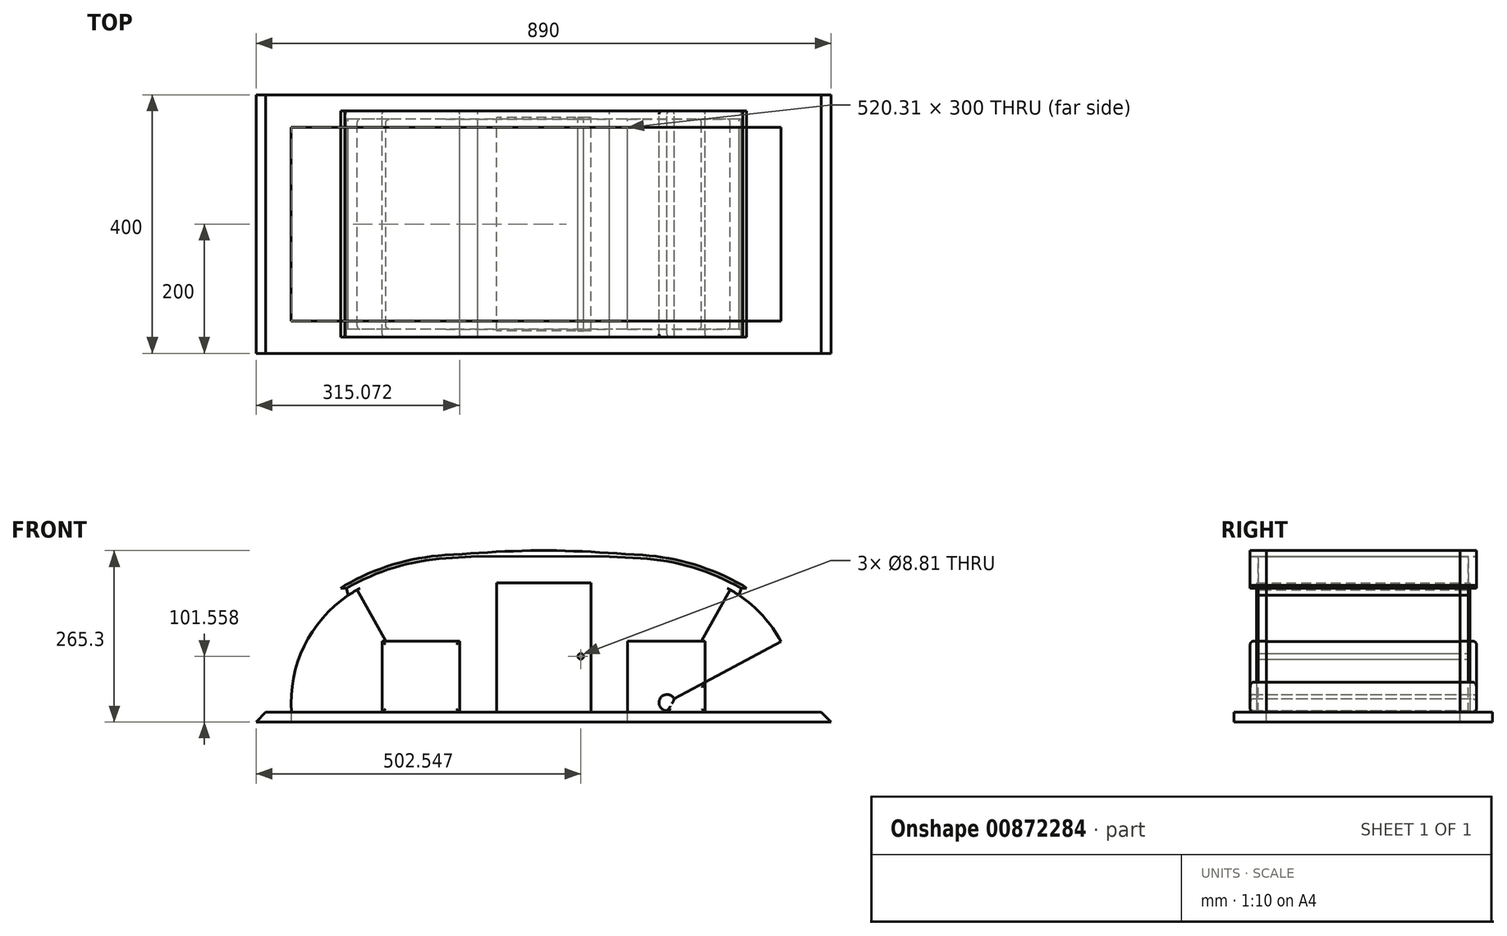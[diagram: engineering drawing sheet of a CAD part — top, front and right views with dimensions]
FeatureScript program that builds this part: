
annotation { "Feature Type Name" : "Feature", "Feature Type Description" : "" }
export const myFeature = defineFeature(function(context is Context, id is Id, definition is map)
    precondition{}
    {
        {
            var Q0;
            Q0=qCreatedBy(makeId("Front.planeOp"),FACE);
            var sketch = newSketch(context, id + "F0", { "sketchPlane" : qUnion([Q0])});
            skLineSegment(sketch, "E0.bottom", {"start": v(0.23, -0.16) * mm, "end": v(250.23, -0.16) * mm});
            skLineSegment(sketch, "E1", {"start": v(250.23, -0.16) * mm, "end": v(190.23, -0.16) * mm});
            skLineSegment(sketch, "E2", {"start": v(250.23, 257.8) * mm, "end": v(249.89, 257.87) * mm});
            skLineSegment(sketch, "E3.bottom", {"start": v(250.23, -0.16) * mm, "end": v(130.23, -0.16) * mm});
            skLineSegment(sketch, "E4", {"start": v(130.23, 109.84) * mm, "end": v(250.23, 109.84) * mm});
            skLineSegment(sketch, "E5", {"start": v(0.23, 199.84) * mm, "end": v(73.25, 199.84) * mm});
            skLineSegment(sketch, "E6", {"start": v(73.25, 199.84) * mm, "end": v(73.25, -0.16) * mm});
            skCircle(sketch, "E7", {"center": v(191.1, 14.84) * mm, "radius": 12.5 * mm});
            skCircle(sketch, "E8", {"center": v(57.55, 86.4) * mm, "radius": 4.4 * mm});
            skArc(sketch, "E9", {"start": v(390.54, -0.16) * mm, "mid": v(362.12, 118.54) * mm, "end": v(270.01, 198.62) * mm});
            skLineSegment(sketch, "E10", {"start": v(250.23, -0.16) * mm, "end": v(390.54, -0.16) * mm});
            skLineSegment(sketch, "E11", {"start": v(191.1, 14.84) * mm, "end": v(390.54, -0.16) * mm, "construction": true});
            skLineSegment(sketch, "E12", {"start": v(0.23, -0.16) * mm, "end": v(553.83, -0.16) * mm});
            skLineSegment(sketch, "E13", {"start": v(191.1, 14.84) * mm, "end": v(197.22, 25.74) * mm});
            skLineSegment(sketch, "E14", {"start": v(191.1, 14.84) * mm, "end": v(367.37, 109.35) * mm});
            skLineSegment(sketch, "E15", {"start": v(190.23, -0.16) * mm, "end": v(250.23, -0.16) * mm});
            skLineSegment(sketch, "E16", {"start": v(250.23, -0.16) * mm, "end": v(250.23, 109.84) * mm});
            skLineSegment(sketch, "E17", {"start": v(190.23, -0.16) * mm, "end": v(130.23, -0.16) * mm});
            skLineSegment(sketch, "E18", {"start": v(130.23, -0.16) * mm, "end": v(130.23, 109.84) * mm});
            skLineSegment(sketch, "E19", {"start": v(0.23, -0.16) * mm, "end": v(0.23, 199.84) * mm});
            skLineSegment(sketch, "E20", {"start": v(302.75, 180.78) * mm, "end": v(305.68, 191.63) * mm});
            skLineSegment(sketch, "E21", {"start": v(-4.12, 211.84) * mm, "end": v(-4.13, 211.84) * mm});
            skArc(sketch, "E22.trimOffspring", {"start": v(305.68, 191.63) * mm, "mid": v(230.69, 224.02) * mm, "end": v(150.23, 238.14) * mm});
            skLineSegment(sketch, "E23", {"start": v(191.1, 14.84) * mm, "end": v(191.1, -0.16) * mm});
            skLineSegment(sketch, "E24", {"start": v(298.85, 183.34) * mm, "end": v(250.23, 107.3) * mm, "construction": true});
            skLineSegment(sketch, "E25", {"start": v(191.1, 14.84) * mm, "end": v(184.4, 25.39) * mm, "construction": true});
            skLineSegment(sketch, "E26", {"start": v(83.85, 183.65) * mm, "end": v(84.52, 182.6) * mm});
            skLineSegment(sketch, "E27", {"start": v(0.23, 199.84) * mm, "end": v(0.23, 213.62) * mm});
            skLineSegment(sketch, "E28", {"start": v(270.01, 198.62) * mm, "end": v(298.76, 198.16) * mm, "construction": true});
            skLineSegment(sketch, "E29", {"start": v(305.68, 191.63) * mm, "end": v(314.05, 191.63) * mm});
            skArc(sketch, "E30.0", {"start": v(308.18, 195.95) * mm, "mid": v(233.4, 228.42) * mm, "end": v(153.2, 242.97) * mm});
            skLineSegment(sketch, "E31", {"start": v(308.18, 195.95) * mm, "end": v(314.05, 191.63) * mm});
            skLineSegment(sketch, "E32.MirrorCS", {"start": v(-72.8, 199.84) * mm, "end": v(-72.8, -0.16) * mm});
            skLineSegment(sketch, "E33.MirrorCS", {"start": v(0.23, 199.84) * mm, "end": v(-72.8, 199.84) * mm});
            skLineSegment(sketch, "E34.MirrorCS", {"start": v(0.23, -0.16) * mm, "end": v(-390.09, -0.16) * mm});
            skArc(sketch, "E35.MirrorCS", {"start": v(-390.09, -0.16) * mm, "mid": v(-366.89, 109.39) * mm, "end": v(-288.45, 189.3) * mm});
            skArc(sketch, "E36.MirrorCS", {"start": v(-307.73, 195.95) * mm, "mid": v(-232.95, 228.42) * mm, "end": v(-152.74, 242.97) * mm});
            skArc(sketch, "E37.MirrorCS", {"start": v(-305.22, 191.63) * mm, "mid": v(-231.06, 223.77) * mm, "end": v(-151.5, 238.04) * mm});
            skLineSegment(sketch, "E38.MirrorCS", {"start": v(-129.77, 109.84) * mm, "end": v(-249.77, 109.84) * mm});
            skLineSegment(sketch, "E39.MirrorCS", {"start": v(-129.77, -0.16) * mm, "end": v(-129.77, 109.84) * mm});
            skLineSegment(sketch, "E40.MirrorCS", {"start": v(-249.77, -0.16) * mm, "end": v(-249.77, 109.84) * mm});
            skLineSegment(sketch, "E41.MirrorCS", {"start": v(-249.77, 46.54) * mm, "end": v(-366.91, 109.35) * mm});
            skLineSegment(sketch, "E42.MirrorCS", {"start": v(-243.9, 109.84) * mm, "end": v(-288.45, 189.3) * mm});
            skFitSpline(sketch, "E43", {"points": [v(-152.74, 242.97) * mm, v(0, 250.14) * mm, v(153.2, 242.97) * mm], "startDerivative": vector(305.6, 21.52) * mm, "endDerivative": vector(306.28, -21.51) * mm});
            skLineSegment(sketch, "E44", {"start": v(150.23, 238.14) * mm, "end": v(102.11, 240.88) * mm});
            skLineSegment(sketch, "E45", {"start": v(-151.5, 238.04) * mm, "end": v(-101.85, 241.43) * mm});
            skLineSegment(sketch, "E46.MirrorCS", {"start": v(-302.3, 180.78) * mm, "end": v(-305.22, 191.63) * mm});
            skLineSegment(sketch, "E47.MirrorCS", {"start": v(-305.22, 191.63) * mm, "end": v(-313.6, 191.63) * mm});
            skLineSegment(sketch, "E48.MirrorCS", {"start": v(-307.73, 195.95) * mm, "end": v(-313.6, 191.63) * mm});
            skLineSegment(sketch, "E49", {"start": v(-101.85, 241.43) * mm, "end": v(102.11, 240.88) * mm});
            skPoint(sketch, "E50.MirrorCS.start.orphan", {"position": v(-298.39, 183.34) * mm});
            skLineSegment(sketch, "E51.trimOffspring", {"start": v(84.52, 182.6) * mm, "end": v(83.85, 183.65) * mm, "construction": true});
            skLineSegment(sketch, "E52.trimOffspring", {"start": v(197.84, 25.37) * mm, "end": v(191.1, 14.84) * mm, "construction": true});
            skLineSegment(sketch, "E53.trimOffspring", {"start": v(244.36, 109.84) * mm, "end": v(288.9, 189.3) * mm});
            skPoint(sketch, "E54.end.orphan", {"position": v(293.87, 198.16) * mm});
            skPoint(sketch, "E55.orphan", {"position": v(-553.37, -0.16) * mm});
            skSolve(sketch);
        }
        {
            var Q0;
            Q0=makeQuery(id+"F0.imprint","IMPRINT",FACE,{"disambiguationData":[TD([[makeQuery(id+"F0.imprint","IMPRINT",EDGE,{"derivedFrom":sQuery(id+"F0.wireOp",EDGE,"E5")}),1.0]])]});
            var Q1;
            {var subQ0=sQuery(id+"F0.wireOp",EDGE,"E39.MirrorCS");Q1=makeQuery(id+"F0.imprint","IMPRINT",FACE,{"disambiguationData":[TD([[makeQuery(id+"F0.imprint","IMPRINT",EDGE,{"derivedFrom":subQ0}),1.0]])]});}
            var Q2;
            {var subQ3=sQuery(id+"F0.wireOp",EDGE,"E41.MirrorCS");Q2=makeQuery(id+"F0.imprint","IMPRINT",FACE,{"disambiguationData":[TD([[makeQuery(id+"F0.imprint","IMPRINT",EDGE,{"derivedFrom":subQ3}),-1.0]])]});}
            var Q3;
            {var subQ5=sQuery(id+"F0.wireOp",EDGE,"E41.MirrorCS");Q3=makeQuery(id+"F0.imprint","IMPRINT",FACE,{"disambiguationData":[TD([[makeQuery(id+"F0.imprint","IMPRINT",EDGE,{"derivedFrom":subQ5}),1.0]])]});}
            var Q4;
            Q4=makeQuery(id+"F0.imprint","IMPRINT",FACE,{"disambiguationData":[TD([[makeQuery(id+"F0.imprint","IMPRINT",EDGE,{"derivedFrom":sQuery(id+"F0.wireOp",EDGE,"E5")}),-1.0]])]});
            var Q5;
            {var subQ0=sQuery(id+"F0.wireOp",EDGE,"E19");Q5=makeQuery(id+"F0.imprint","IMPRINT",FACE,{"disambiguationData":[TD([[makeQuery(id+"F0.imprint","IMPRINT",EDGE,{"derivedFrom":subQ0}),1.0]])]});}
            var Q6;
            {var subQ3=sQuery(id+"F0.wireOp",EDGE,"E53.trimOffspring");Q6=makeQuery(id+"F0.imprint","IMPRINT",FACE,{"disambiguationData":[TD([[makeQuery(id+"F0.imprint","IMPRINT",EDGE,{"derivedFrom":subQ3}),1.0]])]});}
            var Q7;
            {var subQ6=sQuery(id+"F0.wireOp",EDGE,"E53.trimOffspring");Q7=makeQuery(id+"F0.imprint","IMPRINT",FACE,{"disambiguationData":[TD([[makeQuery(id+"F0.imprint","IMPRINT",EDGE,{"derivedFrom":subQ6}),-1.0]])]});}
            var Q8;
            {var subQ0=sQuery(id+"F0.wireOp",EDGE,"E12");var subQ1=sQuery(id+"F0.wireOp",EDGE,"E9");var subQ2=makeQuery(id+"F0.imprint","INTERSECT",VERTEX,{"derivedFrom":[subQ1,subQ0]});Q8=makeQuery(id+"F0.imprint","IMPRINT",FACE,{"disambiguationData":[TD([[makeQuery(id+"F0.imprint","IMPRINT",EDGE,{"disambiguationData":[TD([[subQ2,-1.0]])],"derivedFrom":subQ1}),1.0]])]});}
            var Q9;
            {var subQ5=sQuery(id+"F0.wireOp",EDGE,"E17");Q9=makeQuery(id+"F0.imprint","IMPRINT",FACE,{"disambiguationData":[TD([[makeQuery(id+"F0.imprint","IMPRINT",EDGE,{"derivedFrom":subQ5}),-1.0]])]});}
            var Q10;
            {var subQ0=sQuery(id+"F0.wireOp",EDGE,"E13");Q10=makeQuery(id+"F0.imprint","IMPRINT",FACE,{"disambiguationData":[TD([[makeQuery(id+"F0.imprint","IMPRINT",EDGE,{"derivedFrom":subQ0}),1.0]])]});}
            var Q11;
            {var subQ0=sQuery(id+"F0.wireOp",EDGE,"E13");Q11=makeQuery(id+"F0.imprint","IMPRINT",FACE,{"disambiguationData":[TD([[makeQuery(id+"F0.imprint","IMPRINT",EDGE,{"derivedFrom":subQ0}),-1.0]])]});}
            var Q12;
            {var subQ0=sQuery(id+"F0.wireOp",EDGE,"E14");var subQ1=sQuery(id+"F0.wireOp",EDGE,"E7");var subQ2=makeQuery(id+"F0.imprint","INTERSECT",VERTEX,{"derivedFrom":[subQ1,subQ0]});Q12=makeQuery(id+"F0.imprint","IMPRINT",FACE,{"disambiguationData":[TD([[makeQuery(id+"F0.imprint","IMPRINT",EDGE,{"disambiguationData":[TD([[subQ2,1.0]])],"derivedFrom":subQ1}),1.0]])]});}
            var Q13;
            {var subQ5=sQuery(id+"F0.wireOp",EDGE,"E14");var subQ6=sQuery(id+"F0.wireOp",EDGE,"E7");var subQ7=makeQuery(id+"F0.imprint","INTERSECT",VERTEX,{"derivedFrom":[subQ6,subQ5]});Q13=makeQuery(id+"F0.imprint","IMPRINT",FACE,{"disambiguationData":[TD([[makeQuery(id+"F0.imprint","IMPRINT",EDGE,{"disambiguationData":[TD([[subQ7,1.0]])],"derivedFrom":subQ6}),-1.0]])]});}
            var Q14;
            {var subQ1=sQuery(id+"F0.wireOp",EDGE,"E20");Q14=makeQuery(id+"F0.imprint","IMPRINT",FACE,{"disambiguationData":[TD([[makeQuery(id+"F0.imprint","IMPRINT",EDGE,{"derivedFrom":subQ1}),1.0]])]});}
            var Q15;
            Q15=makeQuery(id+"F0.imprint","IMPRINT",FACE,{"disambiguationData":[TD([[makeQuery(id+"F0.imprint","IMPRINT",EDGE,{"derivedFrom":sQuery(id+"F0.wireOp",EDGE,"E22.trimOffspring")}),-1.0]])]});
            extrude(context, id + "F1", {"entities" : qUnion([Q0, Q1, Q2, Q3, Q4, Q5, Q6, Q7, Q8, Q9, Q10, Q11, Q12, Q13, Q14, Q15]), "endBound" : BoundingType.SYMMETRIC, "depth" : 300 * mm, "offsetDistance" : 25 * mm});
        }
        {
            var Q0;
            Q0=makeQuery(id+"F0.imprint","IMPRINT",FACE,{"disambiguationData":[TD([[makeQuery(id+"F0.imprint","IMPRINT",EDGE,{"derivedFrom":sQuery(id+"F0.wireOp",EDGE,"E22.trimOffspring")}),-1.0]])]});
            extrude(context, id + "F2", {"entities" : qUnion([Q0]), "endBound" : BoundingType.SYMMETRIC, "depth" : 350 * mm, "offsetDistance" : 25 * mm});
        }
        {
            var Q0;
            {var subQ0=sQuery(id+"F0.wireOp",EDGE,"E39.MirrorCS");Q0=makeQuery(id+"F0.imprint","IMPRINT",FACE,{"disambiguationData":[TD([[makeQuery(id+"F0.imprint","IMPRINT",EDGE,{"derivedFrom":subQ0}),1.0]])]});}
            var Q1;
            {var subQ5=sQuery(id+"F0.wireOp",EDGE,"E17");Q1=makeQuery(id+"F0.imprint","IMPRINT",FACE,{"disambiguationData":[TD([[makeQuery(id+"F0.imprint","IMPRINT",EDGE,{"derivedFrom":subQ5}),-1.0]])]});}
            var Q2;
            {var subQ5=sQuery(id+"F0.wireOp",EDGE,"E14");var subQ6=sQuery(id+"F0.wireOp",EDGE,"E7");var subQ7=makeQuery(id+"F0.imprint","INTERSECT",VERTEX,{"derivedFrom":[subQ6,subQ5]});Q2=makeQuery(id+"F0.imprint","IMPRINT",FACE,{"disambiguationData":[TD([[makeQuery(id+"F0.imprint","IMPRINT",EDGE,{"disambiguationData":[TD([[subQ7,1.0]])],"derivedFrom":subQ6}),-1.0]])]});}
            var Q3;
            {var subQ0=sQuery(id+"F0.wireOp",EDGE,"E13");Q3=makeQuery(id+"F0.imprint","IMPRINT",FACE,{"disambiguationData":[TD([[makeQuery(id+"F0.imprint","IMPRINT",EDGE,{"derivedFrom":subQ0}),1.0]])]});}
            var Q4;
            {var subQ0=sQuery(id+"F0.wireOp",EDGE,"E14");var subQ1=sQuery(id+"F0.wireOp",EDGE,"E7");var subQ2=makeQuery(id+"F0.imprint","INTERSECT",VERTEX,{"derivedFrom":[subQ1,subQ0]});Q4=makeQuery(id+"F0.imprint","IMPRINT",FACE,{"disambiguationData":[TD([[makeQuery(id+"F0.imprint","IMPRINT",EDGE,{"disambiguationData":[TD([[subQ2,1.0]])],"derivedFrom":subQ1}),1.0]])]});}
            var Q5;
            {var subQ0=sQuery(id+"F0.wireOp",EDGE,"E13");Q5=makeQuery(id+"F0.imprint","IMPRINT",FACE,{"disambiguationData":[TD([[makeQuery(id+"F0.imprint","IMPRINT",EDGE,{"derivedFrom":subQ0}),-1.0]])]});}
            extrude(context, id + "F3", {"entities" : qUnion([Q0, Q1, Q2, Q3, Q4, Q5]), "endBound" : BoundingType.SYMMETRIC, "depth" : 350 * mm, "offsetDistance" : 25 * mm});
        }
        {
            var Q0;
            {var subQ0=sQuery(id+"F0.wireOp",EDGE,"E19");Q0=makeQuery(id+"F0.imprint","IMPRINT",FACE,{"disambiguationData":[TD([[makeQuery(id+"F0.imprint","IMPRINT",EDGE,{"derivedFrom":subQ0}),1.0]])]});}
            var Q1;
            Q1=makeQuery(id+"F0.imprint","IMPRINT",FACE,{"disambiguationData":[TD([[makeQuery(id+"F0.imprint","IMPRINT",EDGE,{"derivedFrom":sQuery(id+"F0.wireOp",EDGE,"E5")}),-1.0]])]});
            var Q2;
            Q2=makeQuery(id+"F0.imprint","IMPRINT",FACE,{"disambiguationData":[TD([[makeQuery(id+"F0.imprint","IMPRINT",EDGE,{"derivedFrom":sQuery(id+"F0.wireOp",EDGE,"E5")}),1.0]])]});
            var Q3;
            {var subQ1=sQuery(id+"F0.wireOp",EDGE,"E20");Q3=makeQuery(id+"F0.imprint","IMPRINT",FACE,{"disambiguationData":[TD([[makeQuery(id+"F0.imprint","IMPRINT",EDGE,{"derivedFrom":subQ1}),1.0]])]});}
            var Q4;
            {var subQ3=sQuery(id+"F0.wireOp",EDGE,"E53.trimOffspring");Q4=makeQuery(id+"F0.imprint","IMPRINT",FACE,{"disambiguationData":[TD([[makeQuery(id+"F0.imprint","IMPRINT",EDGE,{"derivedFrom":subQ3}),1.0]])]});}
            extrude(context, id + "F4", {"entities" : qUnion([Q0, Q1, Q2, Q3, Q4]), "endBound" : BoundingType.SYMMETRIC, "depth" : 325 * mm, "offsetDistance" : 25 * mm});
        }
        {
            var Q0;
            {var subQ0=sQuery(id+"F0.wireOp",EDGE,"E19");Q0=makeQuery(id+"F0.imprint","IMPRINT",FACE,{"disambiguationData":[TD([[makeQuery(id+"F0.imprint","IMPRINT",EDGE,{"derivedFrom":subQ0}),1.0]])]});}
            var Q1;
            Q1=makeQuery(id+"F0.imprint","IMPRINT",FACE,{"disambiguationData":[TD([[makeQuery(id+"F0.imprint","IMPRINT",EDGE,{"derivedFrom":sQuery(id+"F0.wireOp",EDGE,"E5")}),-1.0]])]});
            extrude(context, id + "F5", {"entities" : qUnion([Q0, Q1]), "endBound" : BoundingType.SYMMETRIC, "depth" : 330 * mm, "offsetDistance" : 25 * mm});
        }
        {
            var Q0;
            Q0=makeQuery(id+"F3.opExtrude","CAP_FACE",FACE,{"disambiguationData":[OSD([sQuery(id+"F0.wireOp",EDGE,"E4"),sQuery(id+"F0.wireOp",EDGE,"E15"),sQuery(id+"F0.wireOp",EDGE,"E16"),sQuery(id+"F0.wireOp",EDGE,"E17"),sQuery(id+"F0.wireOp",EDGE,"E18")])],"isStart":true});
            var Q1;
            Q1=makeQuery(id+"F3.opExtrude","CAP_FACE",FACE,{"disambiguationData":[OSD([sQuery(id+"F0.wireOp",EDGE,"E34.MirrorCS"),sQuery(id+"F0.wireOp",EDGE,"E38.MirrorCS"),sQuery(id+"F0.wireOp",EDGE,"E39.MirrorCS"),sQuery(id+"F0.wireOp",EDGE,"E40.MirrorCS")])],"isStart":true});
            var Q2;
            Q2=makeQuery(id+"F3.opExtrude","CAP_FACE",FACE,{"disambiguationData":[OSD([sQuery(id+"F0.wireOp",EDGE,"E34.MirrorCS"),sQuery(id+"F0.wireOp",EDGE,"E38.MirrorCS"),sQuery(id+"F0.wireOp",EDGE,"E39.MirrorCS"),sQuery(id+"F0.wireOp",EDGE,"E40.MirrorCS")])],"isStart":false});
            var Q3;
            Q3=makeQuery(id+"F3.opExtrude","CAP_FACE",FACE,{"disambiguationData":[OSD([sQuery(id+"F0.wireOp",EDGE,"E4"),sQuery(id+"F0.wireOp",EDGE,"E15"),sQuery(id+"F0.wireOp",EDGE,"E16"),sQuery(id+"F0.wireOp",EDGE,"E17"),sQuery(id+"F0.wireOp",EDGE,"E18")])],"isStart":false});
            var Q4;
            Q4=makeQuery(id+"F4.opExtrude","CAP_EDGE",EDGE,{"disambiguationData":[OSD([sQuery(id+"F0.wireOp",EDGE,"E53.trimOffspring")])],"isStart":true});
            var Q5;
            Q5=makeQuery(id+"F4.opExtrude","CAP_EDGE",EDGE,{"disambiguationData":[OSD([sQuery(id+"F0.wireOp",EDGE,"E53.trimOffspring")])],"isStart":false});
            var Q6;
            Q6=makeQuery(id+"F4.opExtrude","CAP_EDGE",EDGE,{"disambiguationData":[OSD([sQuery(id+"F0.wireOp",EDGE,"E42.MirrorCS")])],"isStart":false});
            var Q7;
            Q7=makeQuery(id+"F4.opExtrude","CAP_EDGE",EDGE,{"disambiguationData":[OSD([sQuery(id+"F0.wireOp",EDGE,"E42.MirrorCS")])],"isStart":true});
            fillet(context, id + "F6", {"entities" : qUnion([Q0, Q1, Q2, Q3, Q4, Q5, Q6, Q7]), "radius" : 5 * mm, "tangentPropagation" : true, "allowEdgeOverflow" : false});
        }
        {
            var Q0;
            Q0=makeQuery(id+"F1.opExtrude","SWEPT_FACE",FACE,{"disambiguationData":[OSD([sQuery(id+"F0.wireOp",EDGE,"E12"),sQuery(id+"F0.wireOp",EDGE,"E15"),sQuery(id+"F0.wireOp",EDGE,"E17"),sQuery(id+"F0.wireOp",EDGE,"E34.MirrorCS")])]});
            var sketch = newSketch(context, id + "F7", { "sketchPlane" : qUnion([Q0])});
            skLineSegment(sketch, "E56.bottom", {"start": v(-450, 200) * mm, "end": v(450, 200) * mm});
            skLineSegment(sketch, "E56.top", {"start": v(-450, -200) * mm, "end": v(450, -200) * mm});
            skLineSegment(sketch, "E56.left", {"start": v(-450, 200) * mm, "end": v(-450, -200) * mm});
            skLineSegment(sketch, "E56.right", {"start": v(450, 200) * mm, "end": v(450, -200) * mm});
            skPoint(sketch, "E56.middle", {"position": v(0, 0) * mm});
            skSolve(sketch);
        }
        {
            var Q0;
            Q0=makeQuery(id+"F7.imprint","IMPRINT",FACE,{"disambiguationData":[TD([[makeQuery(id+"F7.imprint","IMPRINT",EDGE,{"derivedFrom":sQuery(id+"F7.wireOp",EDGE,"E56.bottom")}),-1.0]])]});
            extrude(context, id + "F8", {"entities" : qUnion([Q0]), "depth" : 15 * mm, "offsetDistance" : 25 * mm});
        }
        {
            var Q0;
            Q0=makeQuery(id+"F8.opExtrude","CAP_EDGE",EDGE,{"disambiguationData":[OSD([sQuery(id+"F7.wireOp",EDGE,"E56.right")])],"isStart":true});
            var Q1;
            Q1=makeQuery(id+"F8.opExtrude","CAP_EDGE",EDGE,{"disambiguationData":[OSD([sQuery(id+"F7.wireOp",EDGE,"E56.left")])],"isStart":true});
            chamfer(context, id + "F9", {"entities" : qUnion([Q0, Q1]), "width" : 20 * mm, "tangentPropagation" : true});
        }
        {
            var Q0;
            Q0=makeQuery(id+"F1.opExtrude","SWEPT_FACE",FACE,{"disambiguationData":[OSD([sQuery(id+"F0.wireOp",EDGE,"E12"),sQuery(id+"F0.wireOp",EDGE,"E15"),sQuery(id+"F0.wireOp",EDGE,"E17"),sQuery(id+"F0.wireOp",EDGE,"E34.MirrorCS")])]});
            extrude(context, id + "F10", {"entities" : qUnion([Q0]), "depth" : 15 * mm, "offsetDistance" : 25 * mm});
        }
    });
